# Revit family: Totem Table Light
name_source: partatom
category: Lighting Fixtures
units: mm (PartAtom-declared; Revit-internal decimal feet)

## family parameters
Always vertical = Yes
Cut with Voids When Loaded = No
Light Source = Yes
OmniClass Number = 23.80.70.00
OmniClass Title = Lighting
Part Type = Normal
Room Calculation Point = No
Round Connector Dimension = Use Diameter
Shared = No
Work Plane-Based = No

## types (5) — shared parameters
Color Filter = 16777215
Default Elevation = 0' - 0"
Dimming Lamp Color Temperature Shift = <None>
Emit Shape Visible in Rendering = No
Emit from Circle Diameter = 2' - 0"
MATERIAL CABLE = Steel, Paint Finish, Ivory, Glossy
MATERIAL LIGHT PIECE = Cloth, Lamp Shade
MATERIAL LIGHT PIECE ATTACHMENT = Steel, Paint Finish, Ivory, Glossy
MATERIAL ROOF ATTACHMENT PIECE = Steel, Paint Finish, Ivory, Glossy
Photometric Web File = TOTE UPDWN _IESNA2002.IES
Tilt Angle = 180.00°

## per-type parameters (varying)
| type | TOTEM TABLE LIGHT BA | TOTEM TABLE LIGHT BB | TOTEM TABLE LIGHT CA | TOTEM TABLE LIGHT CB | TOTEM TABLE LIGHT CC |
| Totem Table Light BA | Yes | No | No | No | No |
| Totem Table Light BB | No | Yes | No | No | No |
| Totem Table Light CA | No | No | Yes | No | No |
| Totem Table Light CB | No | No | No | Yes | No |
| Totem Table Light CC | No | No | No | No | Yes |

## geometry (parser evidence)
native form markers: Sweep x2
no freeform markers — native parametric forms only
